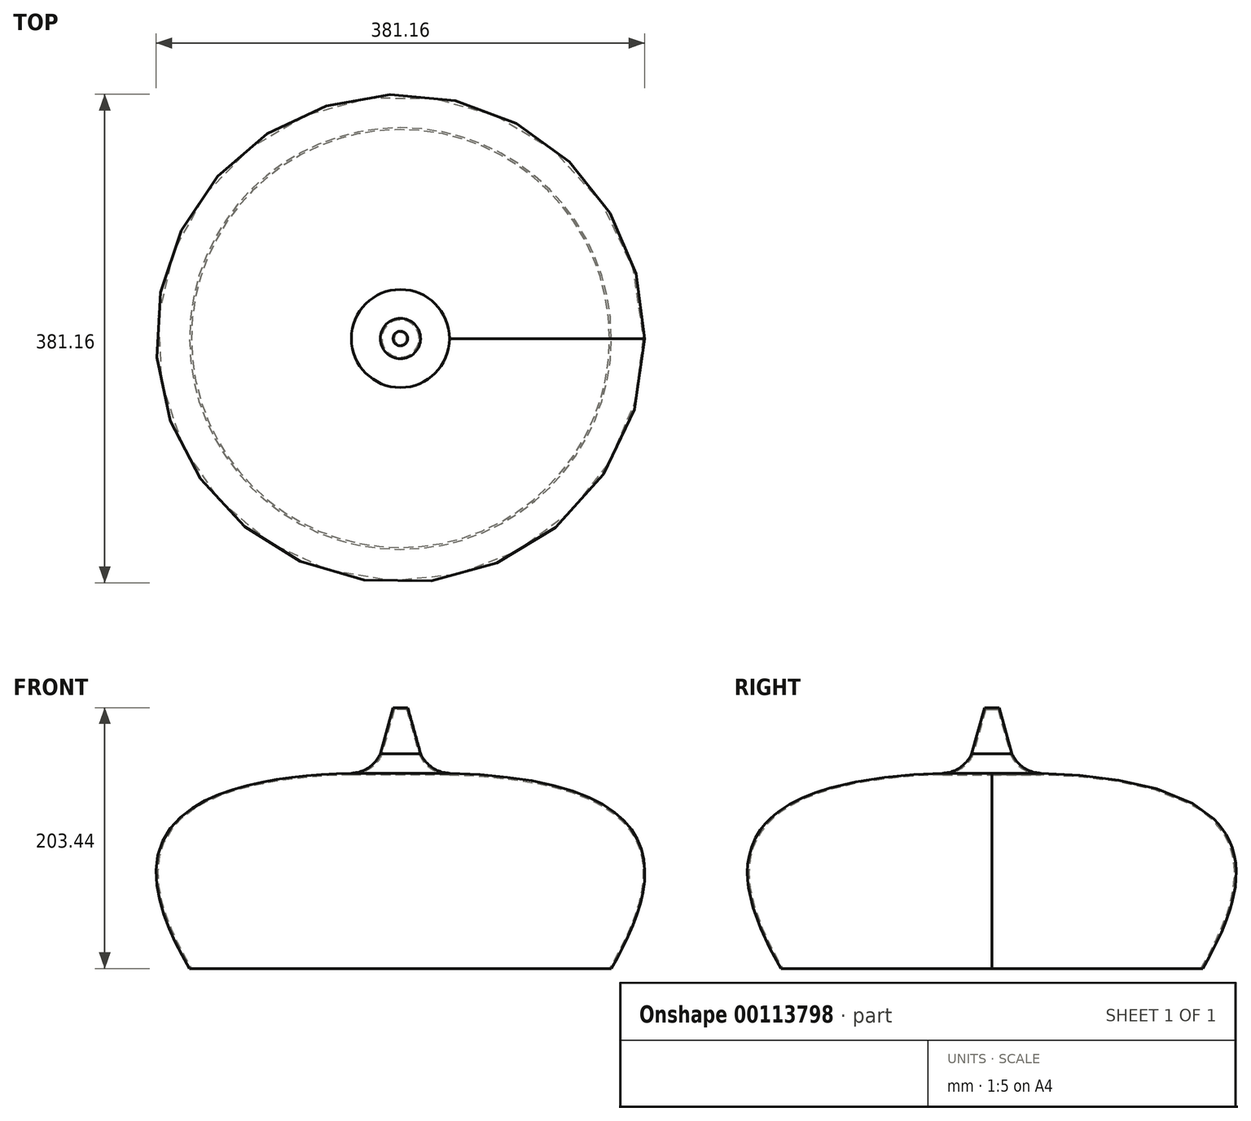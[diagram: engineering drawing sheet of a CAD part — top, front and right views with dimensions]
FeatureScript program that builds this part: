
annotation { "Feature Type Name" : "Feature", "Feature Type Description" : "" }
export const myFeature = defineFeature(function(context is Context, id is Id, definition is map)
    precondition{}
    {
        {
            var Q0;
            Q0=qCreatedBy(makeId("Front.planeOp"),FACE);
            var sketch = newSketch(context, id + "F0", { "sketchPlane" : qUnion([Q0])});
            skLineSegment(sketch, "E0.left", {"start": v(191.12, -75.92) * mm, "end": v(189.47, 127.27) * mm, "construction": true});
            skLineSegment(sketch, "E0.right", {"start": v(-189.88, -76.47) * mm, "end": v(-191.12, 75.92) * mm, "construction": true});
            skPoint(sketch, "E0.middle", {"position": v(0, 0) * mm});
            skLineSegment(sketch, "E1", {"start": v(-189.88, -76.47) * mm, "end": v(-164.48, -76.44) * mm, "construction": true});
            skFitSpline(sketch, "E2", {"points": [v(-19.67, 76.24) * mm, v(-164.48, -76.44) * mm], "startDerivative": vector(-636.27, -0.97) * mm, "endDerivative": vector(109.1, -188.72) * mm});
            skLineSegment(sketch, "E3", {"start": v(-164.48, -76.44) * mm, "end": v(0, -76.2) * mm});
            skPoint(sketch, "E4.newPointB", {"position": v(189.88, 76.47) * mm});
            skArc(sketch, "E5.filletArc", {"start": v(-38.27, 75.97) * mm, "mid": v(-24.77, 80.32) * mm, "end": v(-15.7, 91.22) * mm});
            skLineSegment(sketch, "E6", {"start": v(0, 127) * mm, "end": v(-5.73, 127) * mm});
            skLineSegment(sketch, "E7", {"start": v(-15.7, 91.22) * mm, "end": v(-5.73, 127) * mm});
            skLineSegment(sketch, "E8", {"start": v(0, 127) * mm, "end": v(0, -76.2) * mm});
            skLineSegment(sketch, "E9.trimOffspring", {"start": v(0, -76.2) * mm, "end": v(-189.88, -76.47) * mm, "construction": true});
            skPoint(sketch, "E0.bottom.end.orphan", {"position": v(0.62, -76.2) * mm});
            skSolve(sketch);
        }
        {
            var Q0;
            Q0=makeQuery(id+"F0.imprint","IMPRINT",FACE,{"disambiguationData":[TD([[makeQuery(id+"F0.imprint","IMPRINT",EDGE,{"derivedFrom":sQuery(id+"F0.wireOp",EDGE,"E2")}),1.0]])]});
            var Q1;
            Q1=sQuery(id+"F0.wireOp",EDGE,"E8");
            revolve(context, id + "F1", {"entities" : qUnion([Q0]), "axis" : qUnion([Q1]), "revolveType" : RevolveType.FULL});
        }
        {
            var Q0;
            Q0=makeQuery(id+"F1.opRevolve","SWEPT_FACE",FACE,{"disambiguationData":[OSD([sQuery(id+"F0.wireOp",EDGE,"E3")])]});
            shell(context, id + "F2", {"entities" : qUnion([Q0]), "thickness" : 1.27 * mm});
        }
    });
